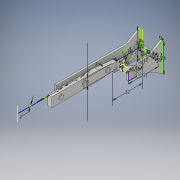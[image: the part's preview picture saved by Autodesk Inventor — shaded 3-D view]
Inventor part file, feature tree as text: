
AUTODESK INVENTOR PART (.ipt)
format: ipt  version: 2019 (Build 230136000, 136)  size: 494,592 bytes
history: native  units: in
note: dims shown in document units (in); Inventor stores cm internally (conversion verified against a paired STEP export)
features: extrude x25, sketch x23
ambient origin geometry x8: Origin, YZ Plane, XZ Plane, XY Plane, X Axis, Y Axis, Z Axis, Center Point
bodies: Solid1 (feature_tree)
feature tree (48):
  sketch  "Sketch1"  dims[d3=0.3346in d4=0.0394in]
  extrude  "Extrusion1"  Depth=0.0394in
  extrude  "Extrusion2"  Depth=0.0787in
  extrude  "Extrusion3"  Depth=0.0394in
  extrude  "Extrusion4"  Depth=0.0787in
  sketch  "Sketch3"  dims[d7=0.0787in d8=0.0394in]
  sketch  "Sketch4"  dims[d9=0.0394in d10=0.0787in]
  extrude  "Extrusion5"  Depth=0.0787in
  sketch  "Sketch5"  dims[d11=0.0787in d12=0.0787in]
  extrude  "Extrusion6"  Depth=0.0787in
  extrude  "Extrusion7"  Depth=0.0787in
  sketch  "Sketch7"  dims[d15=0.0787in d16=0.0787in]
  extrude  "Extrusion8"  Depth=0.9843in TaperAngle=0.0deg
  extrude  "Extrusion9"  Depth=0.2362in TaperAngle=0.0deg
  sketch  "Sketch10"  dims[d17=0.0787in d18=0.9843in d19=0.0in]
  extrude  "Extrusion12"  Depth=0.0787in TaperAngle=0.0deg
  extrude  "Extrusion13"  Depth=0.1181in
  sketch  "Sketch11"  dims[d20=0.1181in d21=0.0in d22=0.2362in d23=0.0in]
  extrude  "Extrusion14"  TaperAngle=45.0deg  [1 undecoded]
  sketch  "Sketch13"  dims[d28=0.1181in d29=0.0in d30=0.4724in]
  extrude  "Extrusion21"  Depth=0.0787in
  extrude  "Extrusion22"  TaperAngle=45.0deg  [1 undecoded]
  extrude  "Extrusion23"  Depth=0.0787in
  extrude  "Extrusion24"  Depth=0.3937in TaperAngle=0.0deg
  extrude  "Extrusion25"  Depth=0.0787in
  extrude  "Extrusion26"  Depth=0.0787in
  sketch  "Sketch24"  dims[d63=0.2362in d64=0.0787in]
  sketch  "Sketch25"  dims[d65=0.2362in d66=0.0787in]
  extrude  "Extrusion27"  Depth=0.0787in
  extrude  "Extrusion28"  Depth=0.0787in
  sketch  "Sketch26"  dims[d67=1.1811in d68=0.0787in]
  extrude  "Extrusion29"  Depth=0.9843in TaperAngle=0.0deg
  extrude  "Extrusion30"  TaperAngle=30.0deg  [1 undecoded]
  extrude  "Extrusion31"  Depth=0.1575in TaperAngle=0.0deg
  extrude  "Extrusion32"  Depth=0.0787in
  extrude  "Extrusion33"  Depth=0.0787in
  sketch  "Sketch2"  dims[d5=0.6693in d6=0.0787in]
  sketch  "Sketch6"  dims[d13=0.0787in d14=0.0787in]
  sketch  "Sketch12"  dims[d25=0.0512in d26=0.0787in d27=0.0in]
  sketch  "Sketch18"  dims[d31=45.0deg d32=45.0deg]
  sketch  "Sketch19"  dims[d33=0.0787in d34=0.0in d35=0.4724in]
  sketch  "Sketch20"  dims[d36=90.0deg d37=45.0deg]
  sketch  "Sketch21"  dims[d38=0.0787in d39=0.0in d40=0.0709in]
  sketch  "Sketch22"  dims[d41=0.1575in d42=0.3937in d43=0.0in]
  sketch  "Sketch23"  dims[d44=2.3622in d45=0.0in d62=0.0787in]
  sketch  "Sketch27"  dims[d69=1.1811in d70=0.9843in d71=0.0in]
  sketch  "Sketch28"  dims[d72=5.1181in d73=0.0in d74=30.0deg]
  sketch  "Sketch29"  dims[d75=30.0deg d76=5.1181in d77=0.0in d79=0.0787in d80=0.0787in d81=0.0787in d82=0.0787in d83=0.0787in d106=1.9685in d107=0.3937in d108=0.1575in d109=0.0in d110=0.1575in d111=0.0in d112=0.1969in d113=0.9843in d114=0.1969in d115=0.9843in d116=0.1969in d117=0.1575in d118=0.0in d131=0.0787in d132=0.0787in d133=0.0787in d134=0.0787in d135=0.0787in d136=0.0787in d137=0.0787in d138=0.0787in d139=0.0787in d140=0.0787in d141=0.0787in d142=0.0787in d143=0.0787in d144=0.0787in d145=0.0787in d146=0.0787in d147=0.0787in d148=0.0in d149=0.0787in d150=0.0787in d151=0.0787in d152=0.0787in d153=0.0787in d154=0.0787in d155=0.0787in d156=0.0787in d157=0.0787in d158=0.0in d159=1.5748in d160=0.5906in d161=0.1969in d162=0.0in d163=1.2598in d164=0.315in d165=0.4724in d166=0.0787in d167=0.0in d168=0.0787in d169=0.0in d170=1.2598in d171=0.4724in d172=0.0787in d173=0.0in d174=0.0787in d175=0.0in d176=0.6299in d177=0.6693in d178=0.0in d179=0.6693in d180=0.0in d181=0.0394in d182=0.0394in d183=0.1575in d184=0.0in]
note: 3 required parameter values undecoded (feature->parameter linkage not recoverable at this tier; creation-order binding heuristic only, values carry confidence <= 0.55)
